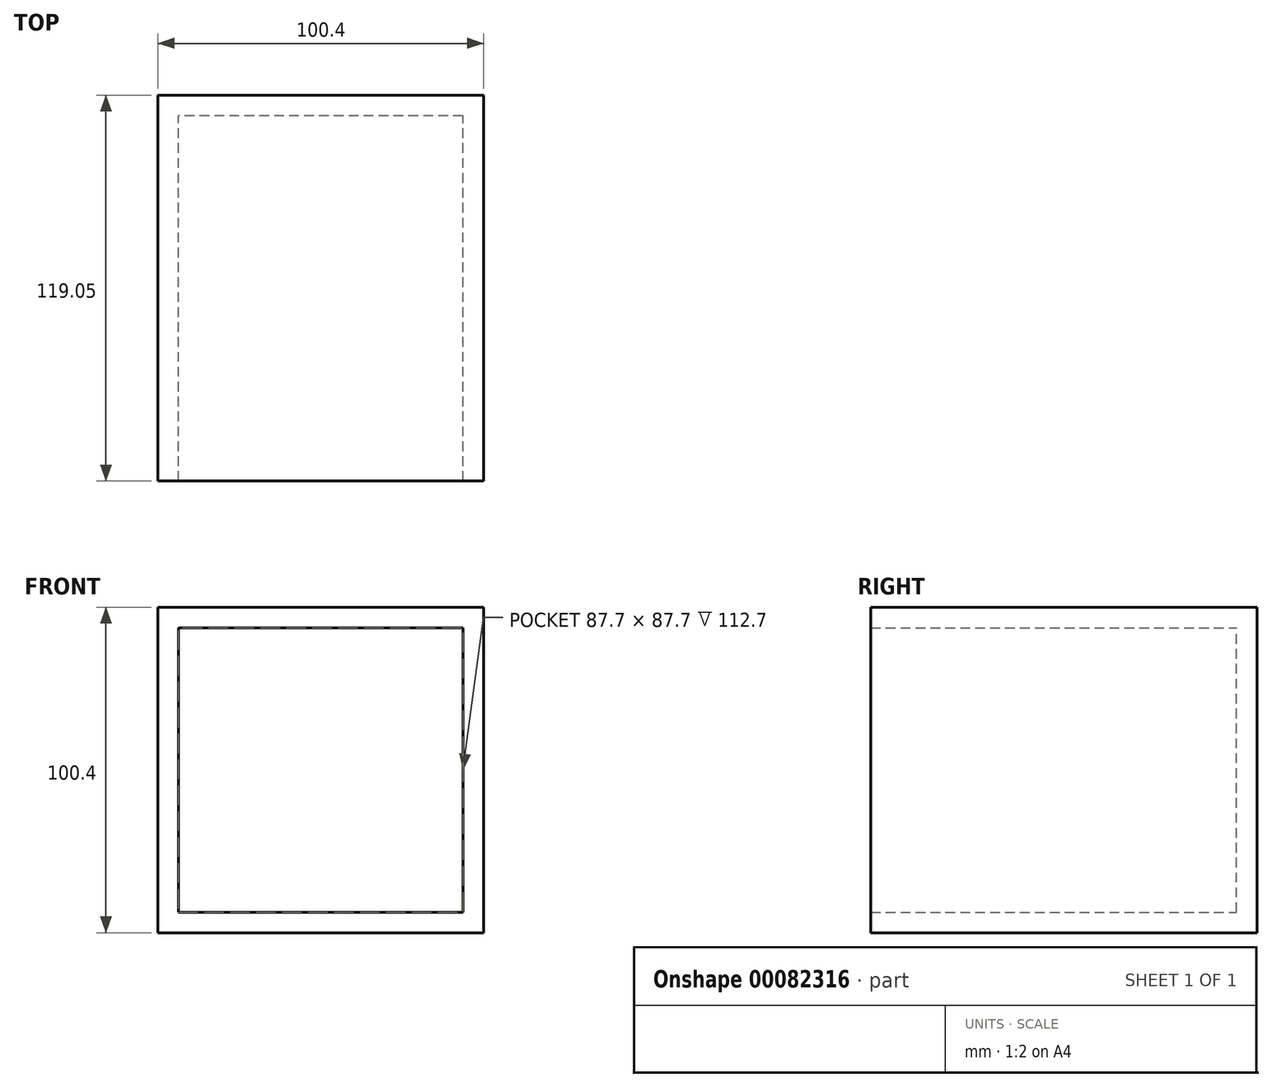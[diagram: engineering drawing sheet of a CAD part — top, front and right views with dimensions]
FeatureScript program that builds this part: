
annotation { "Feature Type Name" : "Feature", "Feature Type Description" : "" }
export const myFeature = defineFeature(function(context is Context, id is Id, definition is map)
    precondition{}
    {
        {
            var Q0;
            Q0=qCreatedBy(makeId("Front.planeOp"),FACE);
            var sketch = newSketch(context, id + "F0", { "sketchPlane" : qUnion([Q0])});
            skLineSegment(sketch, "E0.bottom", {"start": v(-43.85, 94.05) * mm, "end": v(43.85, 94.05) * mm});
            skLineSegment(sketch, "E0.top", {"start": v(-43.85, 6.35) * mm, "end": v(43.85, 6.35) * mm});
            skLineSegment(sketch, "E0.left", {"start": v(-43.85, 94.05) * mm, "end": v(-43.85, 6.35) * mm});
            skLineSegment(sketch, "E0.right", {"start": v(43.85, 94.05) * mm, "end": v(43.85, 6.35) * mm});
            skLineSegment(sketch, "E1.bottom", {"start": v(-50.2, 100.4) * mm, "end": v(50.2, 100.4) * mm});
            skLineSegment(sketch, "E1.top", {"start": v(-50.2, 0) * mm, "end": v(50.2, 0) * mm});
            skLineSegment(sketch, "E1.left", {"start": v(-50.2, 100.4) * mm, "end": v(-50.2, 0) * mm});
            skLineSegment(sketch, "E1.right", {"start": v(50.2, 100.4) * mm, "end": v(50.2, 0) * mm});
            skLineSegment(sketch, "E2", {"start": v(-43.85, 94.05) * mm, "end": v(-43.85, 100.4) * mm, "construction": true});
            skLineSegment(sketch, "E3", {"start": v(-43.85, 94.05) * mm, "end": v(-50.2, 94.05) * mm, "construction": true});
            skLineSegment(sketch, "E4", {"start": v(43.85, 6.35) * mm, "end": v(50.2, 6.35) * mm, "construction": true});
            skLineSegment(sketch, "E5", {"start": v(43.85, 6.35) * mm, "end": v(43.85, 0) * mm, "construction": true});
            skPoint(sketch, "E6", {"position": v(0, 0) * mm});
            skLineSegment(sketch, "E7", {"start": v(0, 50.2) * mm, "end": v(0, 94.05) * mm, "construction": true});
            skLineSegment(sketch, "E8", {"start": v(0, 50.2) * mm, "end": v(-43.85, 50.2) * mm, "construction": true});
            skSolve(sketch);
        }
        {
            var Q0;
            Q0=makeQuery(id+"F0.imprint","IMPRINT",FACE,{"disambiguationData":[TD([[makeQuery(id+"F0.imprint","IMPRINT",EDGE,{"derivedFrom":sQuery(id+"F0.wireOp",EDGE,"E0.bottom")}),1.0]])]});
            var Q1;
            Q1=makeQuery(id+"F0.imprint","IMPRINT",FACE,{"disambiguationData":[TD([[makeQuery(id+"F0.imprint","IMPRINT",EDGE,{"derivedFrom":sQuery(id+"F0.wireOp",EDGE,"E0.bottom")}),-1.0]])]});
            extrude(context, id + "F1", {"entities" : qUnion([Q0, Q1]), "depth" : 6.35 * mm});
        }
        {
            var Q0;
            Q0 = qSketchRegion(id + "F0", true);
            extrude(context, id + "F2", {"entities" : qUnion([Q0]), "operationType" : NewBodyOperationType.ADD, "depth" : 100 * mm + 19.05 * mm});
        }
    });
